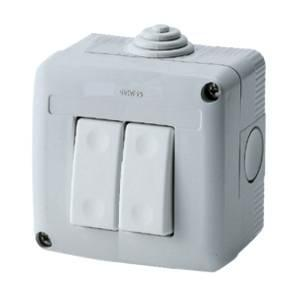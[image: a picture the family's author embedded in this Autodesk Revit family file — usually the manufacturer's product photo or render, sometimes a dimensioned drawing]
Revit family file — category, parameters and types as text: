
# Revit family: Domotics-DomesticRanges-GEWISS-27COMBI_SYSTEM-IP40_COMMAND_1M
name_source: partatom
category: Apparecchi elettrici
revit_build: Autodesk Revit 2016 (Build: 20161004_0715(x64)
units: mm (PartAtom-declared; Revit-internal decimal feet)

## family parameters
Condiviso = Sì
Host = Superficie
Mantenere orientamento annotazione = Sì
Numero OmniClass = 23.80.50.11.14
Punto di calcolo locali = No
Quota connettore circolare = Usa diametro
Taglio con vuoti quando caricato = Sì
Tipo di parte = Normale
Titolo OmniClass = Switches

## types (1)
- Domotics-DomesticRanges-GEWISS-27COMBI_SYSTEM-IP40_COMMAND_1M
    1DEV = Sì
    2DEV = No
    Bidimensionale = bidimensionale system contenitori IP40 completi pulsanti : 1P
    Catalogue = DOMOTICS
    Catalogue Range = 27COMBI
    Characteristics = Halogen free
    Colour = Grey RAL 7035
    Contenitore = SYSTEM CONTENITORI IP40_BASE : GW27001 - 1 posto
    Description: = Push-button 1P NO 10A
    Descrizione = 10A 1P PUSH-BUTTON IP40
    Dimensions LxHxD (mm) = 66x82x55
    EAN code = 8011564095380
    Electrocod = 0130
    Glow Wire Test = 650°C
    IDF = 8b5d4052-f5ae-4c0a-b25e-7516e5a0adab
    IDT = 264e3860-11d5-4595-8a4f-1cc7c44a1a4c
    INT = No
    IP degree = IP40
    Immagine tipo = GW27805.jpg
    Installation temperature = -25 +60 °C
    Insulation class = II
    Larghezza foro = 23 mm  [stored 0.0754593 ft]
    Larghezza scatola = 66 mm  [stored 0.216535 ft]
    Lid screws = Corrosion-resistant steel
    Modello = GW27805
    N. holes Ã˜ 23 with cable gland = 1
    No. knockout holes Ã˜ 23 = 3
    No. knockout holes Ã˜23 = 3 on sides / 1 on the bottom
    Outer dim. LxHxD (mm) = 66x82x55
    Produttore = GEWISS S.p.A.
    Prospetto di default = 1219 mm
    SCATOLA = GEWISS GRIGIO
    SEO = Enclosure
    Simbolo = SIMBOLO CONTENITORI COMPLETI : PUL
    Standard; = EN 60669-1
    Technical sheet = https://www.gewiss.com
    Thermo-pressure with ball = 70
    Tipo Deviatore = SYSTEM DEVIATORI_BASE : GW20576 - DEVIATORE 1P 16AX SY/WT
    Tipo interruttore = SYSTEM INTERRUTTORI_BASE : GW20503 - INTERRUTTORE 2P 16A SY/WT - 0 / 1
    Torque screws tightening = 0,8NM
    Type of knockout holes = Removable with tool
    URL = https://www.gewiss.com
    Version file RFA = 19.4
    Voltage = 230V ac
    Voltage: = 250 V ac

note: source unit labels omitted for Thermo-pressure with ball — the stored unit's dimension contradicts the parameter name (converter mislabeling)

note: [stored X ft] marks values corroborated as IEEE doubles in the binary element streams (Revit-internal decimal feet)

## geometry (parser evidence)
native form markers: Sweep x2
no freeform markers — native parametric forms only
